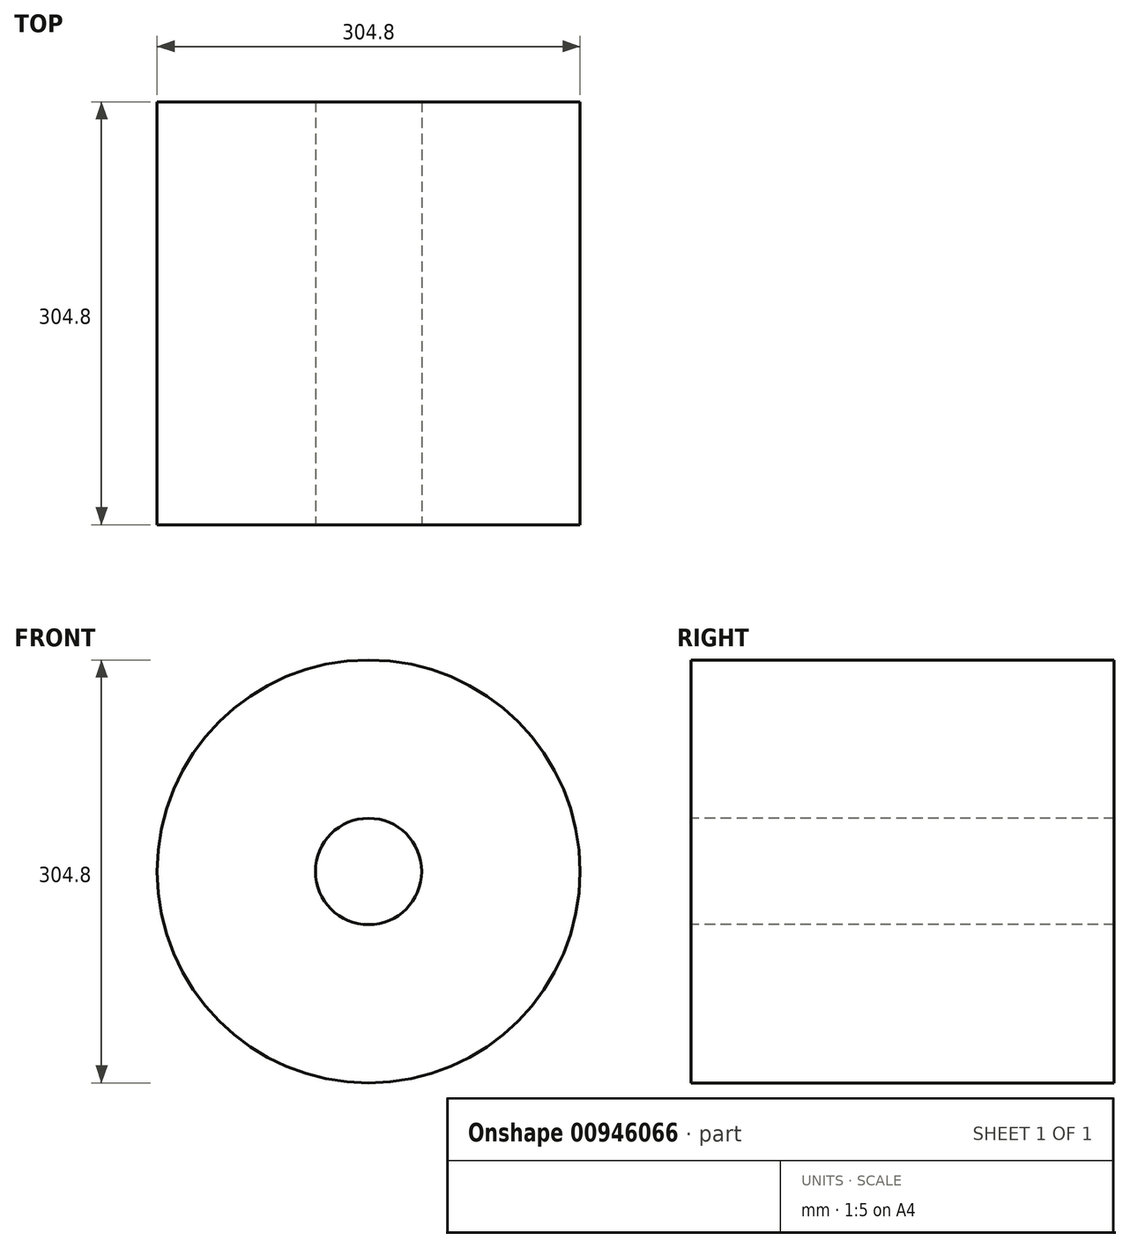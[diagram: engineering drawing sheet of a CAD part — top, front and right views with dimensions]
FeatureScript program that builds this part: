
annotation { "Feature Type Name" : "Feature", "Feature Type Description" : "" }
export const myFeature = defineFeature(function(context is Context, id is Id, definition is map)
    precondition{}
    {
        {
            var Q0;
            Q0=qCreatedBy(makeId("Front.planeOp"),FACE);
            var sketch = newSketch(context, id + "F0", { "sketchPlane" : qUnion([Q0])});
            skCircle(sketch, "E0", {"center": v(0, 0) * mm, "radius": 152.4 * mm});
            skSolve(sketch);
        }
        {
            var Q0;
            Q0=makeQuery(id+"F0.imprint","IMPRINT",FACE,{"disambiguationData":[TD([[makeQuery(id+"F0.imprint","IMPRINT",EDGE,{"derivedFrom":sQuery(id+"F0.wireOp",EDGE,"E0")}),1.0]])]});
            extrude(context, id + "F1", {"entities" : qUnion([Q0]), "depth" : 304.8 * mm, "offsetDistance" : 25.4 * mm});
        }
        {
            var Q0;
            Q0=makeQuery(id+"F1.opExtrude","CAP_FACE",FACE,{"disambiguationData":[OSD([sQuery(id+"F0.wireOp",EDGE,"E0")])],"isStart":false});
            var sketch = newSketch(context, id + "F2", { "sketchPlane" : qUnion([Q0])});
            skCircle(sketch, "E1", {"center": v(0, 0) * mm, "radius": 38.31 * mm});
            skSolve(sketch);
        }
        {
            var Q0;
            Q0=makeQuery(id+"F2.imprint","IMPRINT",FACE,{"disambiguationData":[TD([[makeQuery(id+"F2.imprint","IMPRINT",EDGE,{"derivedFrom":sQuery(id+"F2.wireOp",EDGE,"E1")}),1.0]])]});
            var Q1;
            Q1=makeQuery(id+"F1.opExtrude","SWEPT_FACE",FACE,{"disambiguationData":[OSD([sQuery(id+"F0.wireOp",EDGE,"E0")])]});
            extrude(context, id + "F3", {"entities" : qUnion([Q0]), "operationType" : NewBodyOperationType.REMOVE, "endBound" : BoundingType.THROUGH_ALL, "oppositeDirection" : true, "depth" : 25.4 * mm, "endBoundEntityFace" : qUnion([Q1]), "offsetDistance" : 25.4 * mm});
        }
    });
